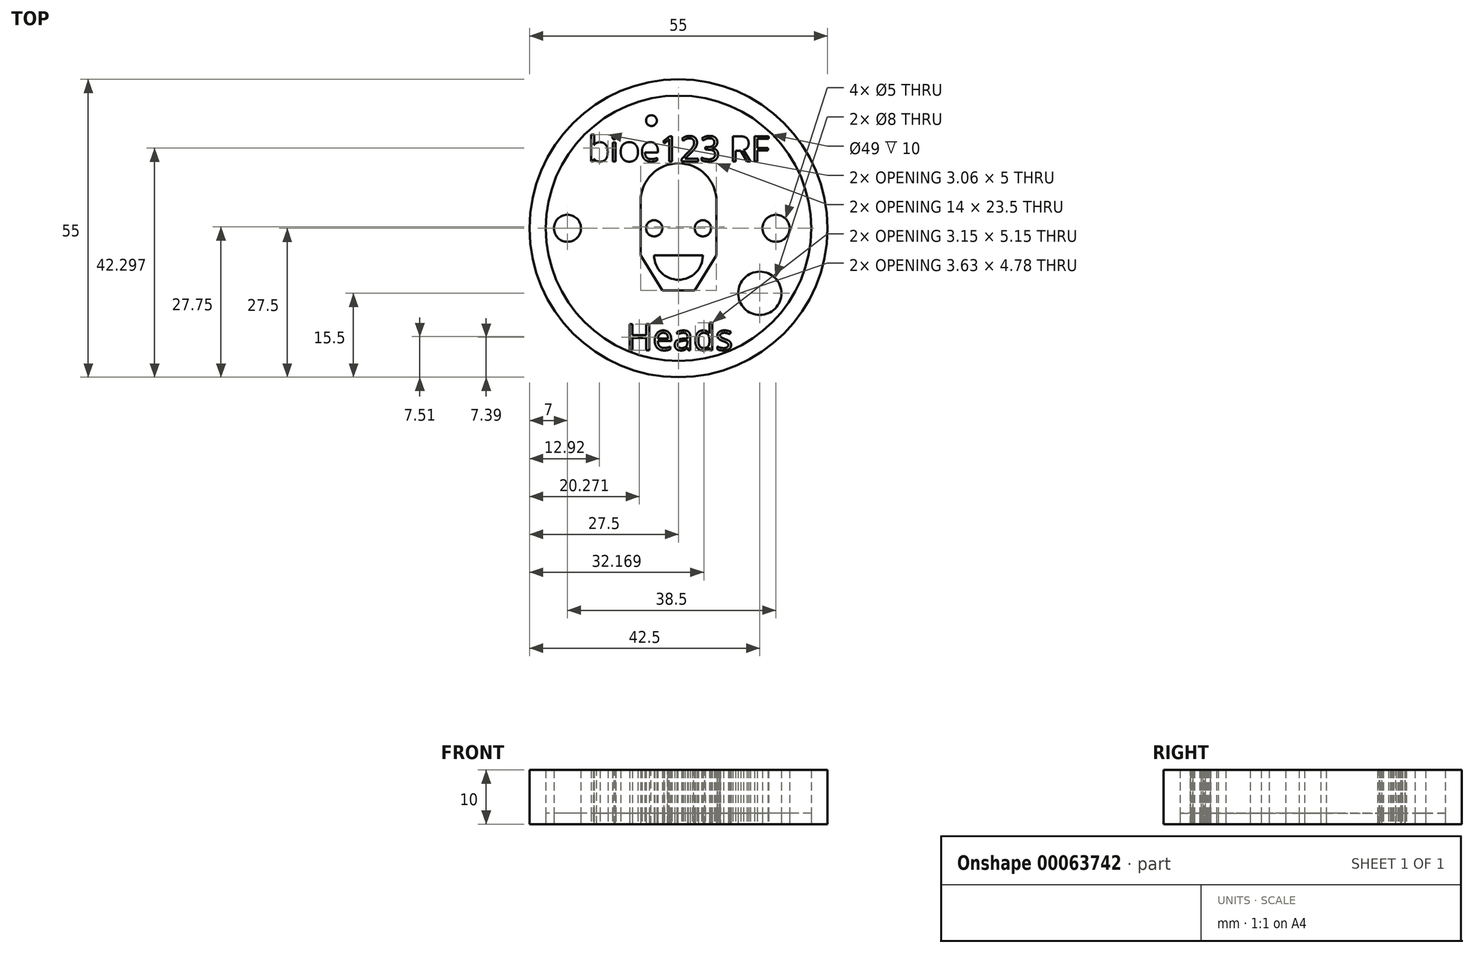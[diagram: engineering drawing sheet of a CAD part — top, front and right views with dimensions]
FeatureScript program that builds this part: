
annotation { "Feature Type Name" : "Feature", "Feature Type Description" : "" }
export const myFeature = defineFeature(function(context is Context, id is Id, definition is map)
    precondition{}
    {
        {
            var Q0;
            Q0=qCreatedBy(makeId("Top.planeOp"),FACE);
            var sketch = newSketch(context, id + "F0", { "sketchPlane" : qUnion([Q0])});
            skCircle(sketch, "E0", {"center": v(0, 0) * mm, "radius": 27.5 * mm});
            skCircle(sketch, "E1", {"center": v(0, 0) * mm, "radius": 24.5 * mm});
            skCircle(sketch, "E2", {"center": v(-5, 19.88) * mm, "radius": 1 * mm});
            skCircle(sketch, "E3", {"center": v(15, -12) * mm, "radius": 4 * mm});
            skCircle(sketch, "E4", {"center": v(-20.5, 0) * mm, "radius": 2.5 * mm});
            skCircle(sketch, "E5", {"center": v(18, 0) * mm, "radius": 2.5 * mm});
            skText(sketch, "E6", { "text": "Heads\n", "fontName": "OpenSans-Regular.ttf"});
            skCircle(sketch, "E7", {"center": v(-4.5, 0) * mm, "radius": 1.5 * mm});
            skCircle(sketch, "E8", {"center": v(4.5, 0) * mm, "radius": 1.5 * mm});
            skLineSegment(sketch, "E9.top", {"start": v(4.5, -5) * mm, "end": v(-4.5, -5) * mm});
            skArc(sketch, "E10", {"start": v(-4.5, -5) * mm, "mid": v(0, -9.5) * mm, "end": v(4.5, -5) * mm});
            skPoint(sketch, "E11.2.internal.snap0", {"position": v(0, -9.5) * mm});
            skLineSegment(sketch, "E12", {"start": v(3, -11.5) * mm, "end": v(7, -5) * mm});
            skLineSegment(sketch, "E13", {"start": v(7, -5) * mm, "end": v(7, 5) * mm});
            skLineSegment(sketch, "E14", {"start": v(-7, 5) * mm, "end": v(-7, -5) * mm});
            skLineSegment(sketch, "E15", {"start": v(-7, -5) * mm, "end": v(-3, -11.5) * mm});
            skLineSegment(sketch, "E16", {"start": v(-3, -11.5) * mm, "end": v(3, -11.5) * mm});
            skLineSegment(sketch, "E17", {"start": v(0, 0) * mm, "end": v(0, -16.05) * mm, "construction": true});
            skArc(sketch, "E18", {"start": v(7, 5) * mm, "mid": v(0, 12) * mm, "end": v(-7, 5) * mm});
            skLineSegment(sketch, "E19", {"start": v(-7, 5) * mm, "end": v(7, 5) * mm, "construction": true});
            skText(sketch, "E20", { "text": "bioe123 RF", "fontName": "OpenSans-Regular.ttf"});
            const initialGuessF0  = {"E6": [-0.0097, -0.0225, 1, 0, 0.00482], "E20": [-0.01667, 0.01236, 1, 0, 0.00468]};
            skSetInitialGuess(sketch, initialGuessF0);
            skSolve(sketch);
        }
        {
            var Q0;
            Q0 = qSketchRegion(id + "F0", true);
            var Q1;
            Q1=makeQuery(id+"F0.imprint","IMPRINT",FACE,{"disambiguationData":[TD([[makeQuery(id+"F0.imprint","IMPRINT",EDGE,{"derivedFrom":sQuery(id+"F0.wireOp",EDGE,"E6.sketch_text.stroke-0")}),-1.0]])]});
            var Q2;
            Q2=makeQuery(id+"F0.imprint","IMPRINT",FACE,{"disambiguationData":[TD([[makeQuery(id+"F0.imprint","IMPRINT",EDGE,{"derivedFrom":sQuery(id+"F0.wireOp",EDGE,"E6.sketch_text.stroke-12")}),-1.0]])]});
            var Q3;
            Q3=makeQuery(id+"F0.imprint","IMPRINT",FACE,{"disambiguationData":[TD([[makeQuery(id+"F0.imprint","IMPRINT",EDGE,{"derivedFrom":sQuery(id+"F0.wireOp",EDGE,"E6.sketch_text.stroke-31")}),-1.0]])]});
            var Q4;
            Q4=makeQuery(id+"F0.imprint","IMPRINT",FACE,{"disambiguationData":[TD([[makeQuery(id+"F0.imprint","IMPRINT",EDGE,{"derivedFrom":sQuery(id+"F0.wireOp",EDGE,"E6.sketch_text.stroke-58")}),-1.0]])]});
            var Q5;
            Q5=makeQuery(id+"F0.imprint","IMPRINT",FACE,{"disambiguationData":[TD([[makeQuery(id+"F0.imprint","IMPRINT",EDGE,{"derivedFrom":sQuery(id+"F0.wireOp",EDGE,"E6.sketch_text.stroke-82")}),-1.0]])]});
            var Q6;
            Q6=makeQuery(id+"F0.imprint","IMPRINT",FACE,{"disambiguationData":[TD([[makeQuery(id+"F0.imprint","IMPRINT",EDGE,{"derivedFrom":sQuery(id+"F0.wireOp",EDGE,"E3")}),1.0]])]});
            var Q7;
            Q7=makeQuery(id+"F0.imprint","IMPRINT",FACE,{"disambiguationData":[TD([[makeQuery(id+"F0.imprint","IMPRINT",EDGE,{"derivedFrom":sQuery(id+"F0.wireOp",EDGE,"E5")}),1.0]])]});
            var Q8;
            Q8=makeQuery(id+"F0.imprint","IMPRINT",FACE,{"disambiguationData":[TD([[makeQuery(id+"F0.imprint","IMPRINT",EDGE,{"derivedFrom":sQuery(id+"F0.wireOp",EDGE,"E7")}),-1.0]])]});
            var Q9;
            Q9=makeQuery(id+"F0.imprint","IMPRINT",FACE,{"disambiguationData":[TD([[makeQuery(id+"F0.imprint","IMPRINT",EDGE,{"derivedFrom":sQuery(id+"F0.wireOp",EDGE,"E4")}),1.0]])]});
            var Q10;
            Q10=makeQuery(id+"F0.imprint","IMPRINT",FACE,{"disambiguationData":[TD([[makeQuery(id+"F0.imprint","IMPRINT",EDGE,{"derivedFrom":sQuery(id+"F0.wireOp",EDGE,"E2")}),1.0]])]});
            extrude(context, id + "F1", {"entities" : qUnion([Q0, Q1, Q2, Q3, Q4, Q5, Q6, Q7, Q8, Q9, Q10]), "depth" : 10 * mm});
        }
        {
            var Q0;
            Q0=makeQuery(id+"F0.imprint","IMPRINT",FACE,{"disambiguationData":[TD([[makeQuery(id+"F0.imprint","IMPRINT",EDGE,{"derivedFrom":sQuery(id+"F0.wireOp",EDGE,"E1")}),1.0]])]});
            var Q1;
            Q1=makeQuery(id+"F0.imprint","IMPRINT",FACE,{"disambiguationData":[TD([[makeQuery(id+"F0.imprint","IMPRINT",EDGE,{"derivedFrom":sQuery(id+"F0.wireOp",EDGE,"E9.top")}),1.0]])]});
            var Q2;
            Q2=makeQuery(id+"F0.imprint","IMPRINT",FACE,{"disambiguationData":[TD([[makeQuery(id+"F0.imprint","IMPRINT",EDGE,{"derivedFrom":sQuery(id+"F0.wireOp",EDGE,"E7")}),1.0]])]});
            var Q3;
            Q3=makeQuery(id+"F0.imprint","IMPRINT",FACE,{"disambiguationData":[TD([[makeQuery(id+"F0.imprint","IMPRINT",EDGE,{"derivedFrom":sQuery(id+"F0.wireOp",EDGE,"E8")}),1.0]])]});
            var Q4;
            Q4=makeQuery(id+"F0.imprint","IMPRINT",FACE,{"disambiguationData":[TD([[makeQuery(id+"F0.imprint","IMPRINT",EDGE,{"derivedFrom":sQuery(id+"F0.wireOp",EDGE,"E6.sketch_text.stroke-26")}),1.0]])]});
            var Q5;
            Q5=makeQuery(id+"F0.imprint","IMPRINT",FACE,{"disambiguationData":[TD([[makeQuery(id+"F0.imprint","IMPRINT",EDGE,{"derivedFrom":sQuery(id+"F0.wireOp",EDGE,"E6.sketch_text.stroke-50")}),1.0]])]});
            var Q6;
            Q6=makeQuery(id+"F0.imprint","IMPRINT",FACE,{"disambiguationData":[TD([[makeQuery(id+"F0.imprint","IMPRINT",EDGE,{"derivedFrom":sQuery(id+"F0.wireOp",EDGE,"E6.sketch_text.stroke-73")}),1.0]])]});
            extrude(context, id + "F2", {"entities" : qUnion([Q0, Q1, Q2, Q3, Q4, Q5, Q6]), "depth" : 2 * mm});
        }
        {
            var Q0;
            Q0=makeQuery(id+"F2.opExtrude","CAP_FACE",FACE,{"disambiguationData":[OSD([sQuery(id+"F0.wireOp",EDGE,"E1"),sQuery(id+"F0.wireOp",EDGE,"E2"),sQuery(id+"F0.wireOp",EDGE,"E3"),sQuery(id+"F0.wireOp",EDGE,"E4"),sQuery(id+"F0.wireOp",EDGE,"E5"),sQuery(id+"F0.wireOp",EDGE,"E6.sketch_text.stroke-0"),sQuery(id+"F0.wireOp",EDGE,"E6.sketch_text.stroke-1"),sQuery(id+"F0.wireOp",EDGE,"E6.sketch_text.stroke-2"),sQuery(id+"F0.wireOp",EDGE,"E6.sketch_text.stroke-3"),sQuery(id+"F0.wireOp",EDGE,"E6.sketch_text.stroke-4"),sQuery(id+"F0.wireOp",EDGE,"E6.sketch_text.stroke-5"),sQuery(id+"F0.wireOp",EDGE,"E6.sketch_text.stroke-6"),sQuery(id+"F0.wireOp",EDGE,"E6.sketch_text.stroke-7"),sQuery(id+"F0.wireOp",EDGE,"E6.sketch_text.stroke-8"),sQuery(id+"F0.wireOp",EDGE,"E6.sketch_text.stroke-9"),sQuery(id+"F0.wireOp",EDGE,"E6.sketch_text.stroke-10"),sQuery(id+"F0.wireOp",EDGE,"E6.sketch_text.stroke-11"),sQuery(id+"F0.wireOp",EDGE,"E6.sketch_text.stroke-12"),sQuery(id+"F0.wireOp",EDGE,"E6.sketch_text.stroke-13"),sQuery(id+"F0.wireOp",EDGE,"E6.sketch_text.stroke-14"),sQuery(id+"F0.wireOp",EDGE,"E6.sketch_text.stroke-15"),sQuery(id+"F0.wireOp",EDGE,"E6.sketch_text.stroke-16"),sQuery(id+"F0.wireOp",EDGE,"E6.sketch_text.stroke-17"),sQuery(id+"F0.wireOp",EDGE,"E6.sketch_text.stroke-18"),sQuery(id+"F0.wireOp",EDGE,"E6.sketch_text.stroke-19"),sQuery(id+"F0.wireOp",EDGE,"E6.sketch_text.stroke-20"),sQuery(id+"F0.wireOp",EDGE,"E6.sketch_text.stroke-21"),sQuery(id+"F0.wireOp",EDGE,"E6.sketch_text.stroke-22"),sQuery(id+"F0.wireOp",EDGE,"E6.sketch_text.stroke-23"),sQuery(id+"F0.wireOp",EDGE,"E6.sketch_text.stroke-24"),sQuery(id+"F0.wireOp",EDGE,"E6.sketch_text.stroke-25"),sQuery(id+"F0.wireOp",EDGE,"E6.sketch_text.stroke-31"),sQuery(id+"F0.wireOp",EDGE,"E6.sketch_text.stroke-32"),sQuery(id+"F0.wireOp",EDGE,"E6.sketch_text.stroke-33"),sQuery(id+"F0.wireOp",EDGE,"E6.sketch_text.stroke-34"),sQuery(id+"F0.wireOp",EDGE,"E6.sketch_text.stroke-35"),sQuery(id+"F0.wireOp",EDGE,"E6.sketch_text.stroke-36"),sQuery(id+"F0.wireOp",EDGE,"E6.sketch_text.stroke-37"),sQuery(id+"F0.wireOp",EDGE,"E6.sketch_text.stroke-38"),sQuery(id+"F0.wireOp",EDGE,"E6.sketch_text.stroke-39"),sQuery(id+"F0.wireOp",EDGE,"E6.sketch_text.stroke-40"),sQuery(id+"F0.wireOp",EDGE,"E6.sketch_text.stroke-41"),sQuery(id+"F0.wireOp",EDGE,"E6.sketch_text.stroke-42"),sQuery(id+"F0.wireOp",EDGE,"E6.sketch_text.stroke-43"),sQuery(id+"F0.wireOp",EDGE,"E6.sketch_text.stroke-44"),sQuery(id+"F0.wireOp",EDGE,"E6.sketch_text.stroke-45"),sQuery(id+"F0.wireOp",EDGE,"E6.sketch_text.stroke-46"),sQuery(id+"F0.wireOp",EDGE,"E6.sketch_text.stroke-47"),sQuery(id+"F0.wireOp",EDGE,"E6.sketch_text.stroke-48"),sQuery(id+"F0.wireOp",EDGE,"E6.sketch_text.stroke-49"),sQuery(id+"F0.wireOp",EDGE,"E6.sketch_text.stroke-58"),sQuery(id+"F0.wireOp",EDGE,"E6.sketch_text.stroke-59"),sQuery(id+"F0.wireOp",EDGE,"E6.sketch_text.stroke-60"),sQuery(id+"F0.wireOp",EDGE,"E6.sketch_text.stroke-61"),sQuery(id+"F0.wireOp",EDGE,"E6.sketch_text.stroke-62"),sQuery(id+"F0.wireOp",EDGE,"E6.sketch_text.stroke-63"),sQuery(id+"F0.wireOp",EDGE,"E6.sketch_text.stroke-64"),sQuery(id+"F0.wireOp",EDGE,"E6.sketch_text.stroke-65"),sQuery(id+"F0.wireOp",EDGE,"E6.sketch_text.stroke-66"),sQuery(id+"F0.wireOp",EDGE,"E6.sketch_text.stroke-67"),sQuery(id+"F0.wireOp",EDGE,"E6.sketch_text.stroke-68"),sQuery(id+"F0.wireOp",EDGE,"E6.sketch_text.stroke-69"),sQuery(id+"F0.wireOp",EDGE,"E6.sketch_text.stroke-70"),sQuery(id+"F0.wireOp",EDGE,"E6.sketch_text.stroke-71"),sQuery(id+"F0.wireOp",EDGE,"E6.sketch_text.stroke-72"),sQuery(id+"F0.wireOp",EDGE,"E6.sketch_text.stroke-82"),sQuery(id+"F0.wireOp",EDGE,"E6.sketch_text.stroke-83"),sQuery(id+"F0.wireOp",EDGE,"E6.sketch_text.stroke-84"),sQuery(id+"F0.wireOp",EDGE,"E6.sketch_text.stroke-85"),sQuery(id+"F0.wireOp",EDGE,"E6.sketch_text.stroke-86"),sQuery(id+"F0.wireOp",EDGE,"E6.sketch_text.stroke-87"),sQuery(id+"F0.wireOp",EDGE,"E6.sketch_text.stroke-88"),sQuery(id+"F0.wireOp",EDGE,"E6.sketch_text.stroke-89"),sQuery(id+"F0.wireOp",EDGE,"E6.sketch_text.stroke-90"),sQuery(id+"F0.wireOp",EDGE,"E6.sketch_text.stroke-91"),sQuery(id+"F0.wireOp",EDGE,"E6.sketch_text.stroke-92"),sQuery(id+"F0.wireOp",EDGE,"E6.sketch_text.stroke-93"),sQuery(id+"F0.wireOp",EDGE,"E6.sketch_text.stroke-94"),sQuery(id+"F0.wireOp",EDGE,"E6.sketch_text.stroke-95"),sQuery(id+"F0.wireOp",EDGE,"E6.sketch_text.stroke-96"),sQuery(id+"F0.wireOp",EDGE,"E6.sketch_text.stroke-97"),sQuery(id+"F0.wireOp",EDGE,"E6.sketch_text.stroke-98"),sQuery(id+"F0.wireOp",EDGE,"E6.sketch_text.stroke-99"),sQuery(id+"F0.wireOp",EDGE,"E6.sketch_text.stroke-100"),sQuery(id+"F0.wireOp",EDGE,"E6.sketch_text.stroke-101"),sQuery(id+"F0.wireOp",EDGE,"E6.sketch_text.stroke-102"),sQuery(id+"F0.wireOp",EDGE,"E6.sketch_text.stroke-103"),sQuery(id+"F0.wireOp",EDGE,"E6.sketch_text.stroke-104"),sQuery(id+"F0.wireOp",EDGE,"E6.sketch_text.stroke-105"),sQuery(id+"F0.wireOp",EDGE,"E6.sketch_text.stroke-106"),sQuery(id+"F0.wireOp",EDGE,"E12"),sQuery(id+"F0.wireOp",EDGE,"E13"),sQuery(id+"F0.wireOp",EDGE,"E14"),sQuery(id+"F0.wireOp",EDGE,"E15"),sQuery(id+"F0.wireOp",EDGE,"E16"),sQuery(id+"F0.wireOp",EDGE,"E18")])],"isStart":false});
            var Q1;
            Q1=makeQuery(id+"F2.opExtrude","CAP_FACE",FACE,{"disambiguationData":[OSD([sQuery(id+"F0.wireOp",EDGE,"E7")])],"isStart":false});
            var Q2;
            Q2=makeQuery(id+"F2.opExtrude","CAP_FACE",FACE,{"disambiguationData":[OSD([sQuery(id+"F0.wireOp",EDGE,"E8")])],"isStart":false});
            var Q3;
            Q3=makeQuery(id+"F2.opExtrude","CAP_FACE",FACE,{"disambiguationData":[OSD([sQuery(id+"F0.wireOp",EDGE,"E9.top"),sQuery(id+"F0.wireOp",EDGE,"E10")])],"isStart":false});
            var Q4;
            Q4=makeQuery(id+"F2.opExtrude","CAP_FACE",FACE,{"disambiguationData":[OSD([sQuery(id+"F0.wireOp",EDGE,"E6.sketch_text.stroke-26"),sQuery(id+"F0.wireOp",EDGE,"E6.sketch_text.stroke-27"),sQuery(id+"F0.wireOp",EDGE,"E6.sketch_text.stroke-28"),sQuery(id+"F0.wireOp",EDGE,"E6.sketch_text.stroke-29"),sQuery(id+"F0.wireOp",EDGE,"E6.sketch_text.stroke-30")])],"isStart":false});
            var Q5;
            Q5=makeQuery(id+"F2.opExtrude","CAP_FACE",FACE,{"disambiguationData":[OSD([sQuery(id+"F0.wireOp",EDGE,"E6.sketch_text.stroke-50"),sQuery(id+"F0.wireOp",EDGE,"E6.sketch_text.stroke-51"),sQuery(id+"F0.wireOp",EDGE,"E6.sketch_text.stroke-52"),sQuery(id+"F0.wireOp",EDGE,"E6.sketch_text.stroke-53"),sQuery(id+"F0.wireOp",EDGE,"E6.sketch_text.stroke-54"),sQuery(id+"F0.wireOp",EDGE,"E6.sketch_text.stroke-55"),sQuery(id+"F0.wireOp",EDGE,"E6.sketch_text.stroke-56"),sQuery(id+"F0.wireOp",EDGE,"E6.sketch_text.stroke-57")])],"isStart":false});
            var Q6;
            Q6=makeQuery(id+"F2.opExtrude","CAP_FACE",FACE,{"disambiguationData":[OSD([sQuery(id+"F0.wireOp",EDGE,"E6.sketch_text.stroke-73"),sQuery(id+"F0.wireOp",EDGE,"E6.sketch_text.stroke-74"),sQuery(id+"F0.wireOp",EDGE,"E6.sketch_text.stroke-75"),sQuery(id+"F0.wireOp",EDGE,"E6.sketch_text.stroke-76"),sQuery(id+"F0.wireOp",EDGE,"E6.sketch_text.stroke-77"),sQuery(id+"F0.wireOp",EDGE,"E6.sketch_text.stroke-78"),sQuery(id+"F0.wireOp",EDGE,"E6.sketch_text.stroke-79"),sQuery(id+"F0.wireOp",EDGE,"E6.sketch_text.stroke-80"),sQuery(id+"F0.wireOp",EDGE,"E6.sketch_text.stroke-81")])],"isStart":false});
            extrude(context, id + "F3", {"entities" : qUnion([Q0, Q1, Q2, Q3, Q4, Q5, Q6]), "depth" : 8 * mm});
        }
    });
